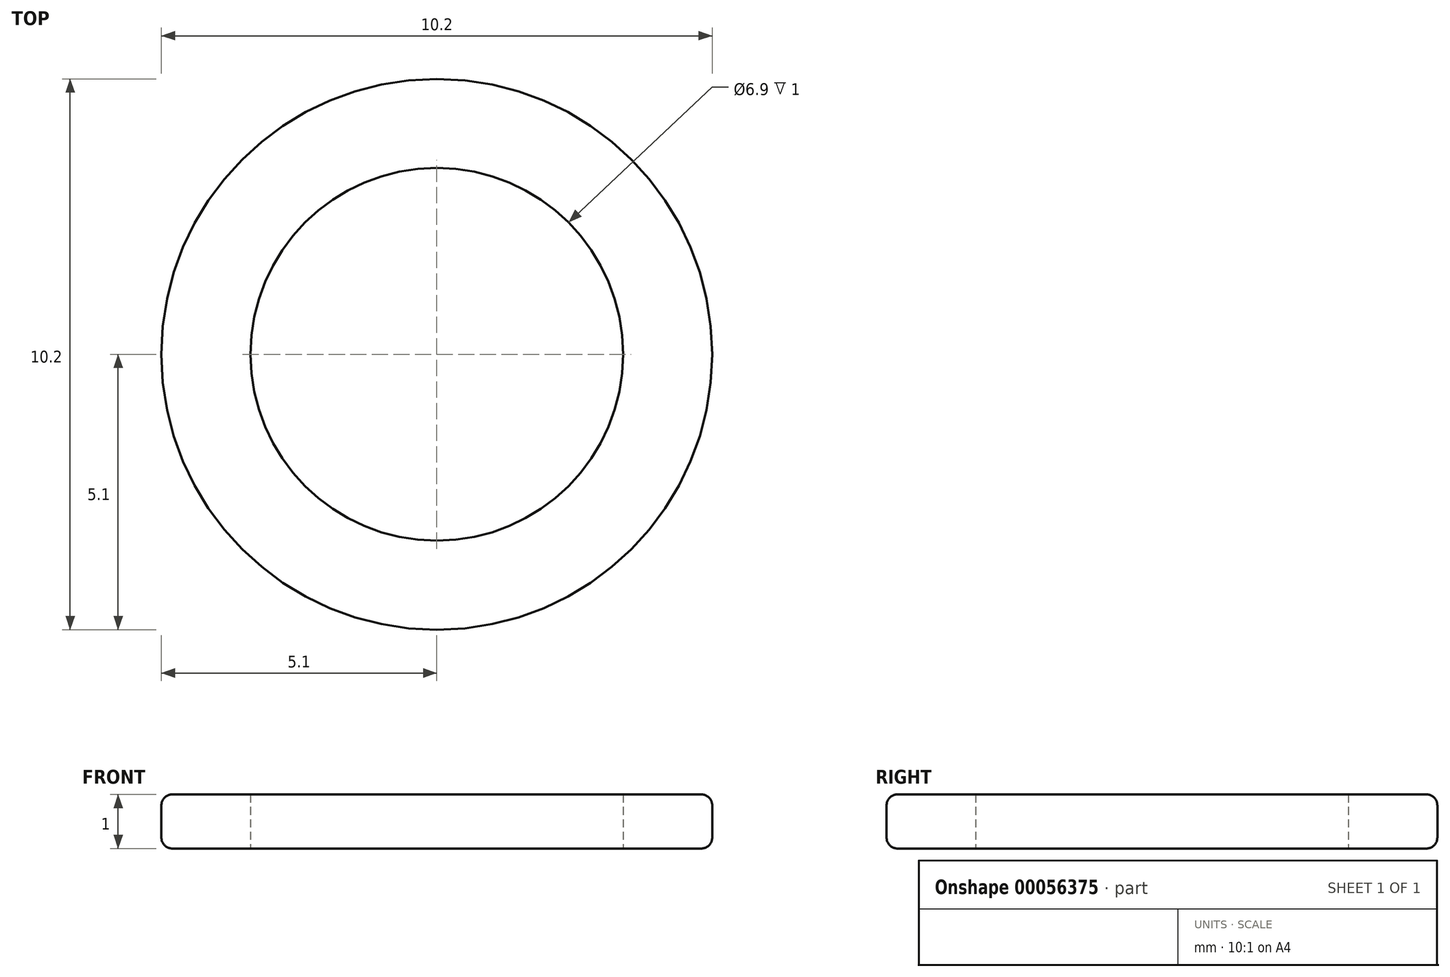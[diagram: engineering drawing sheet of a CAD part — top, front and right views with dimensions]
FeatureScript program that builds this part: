
annotation { "Feature Type Name" : "Feature", "Feature Type Description" : "" }
export const myFeature = defineFeature(function(context is Context, id is Id, definition is map)
    precondition{}
    {
        {
            var Q0;
            Q0=qCreatedBy(makeId("Top.planeOp"),FACE);
            var sketch = newSketch(context, id + "F0", { "sketchPlane" : qUnion([Q0])});
            skCircle(sketch, "E0", {"center": v(0, 0) * mm, "radius": 5.1 * mm});
            skCircle(sketch, "E1", {"center": v(0, 0) * mm, "radius": 3.45 * mm});
            skSolve(sketch);
        }
        {
            var Q0;
            Q0=makeQuery(id+"F0.imprint","IMPRINT",FACE,{"disambiguationData":[TD([[makeQuery(id+"F0.imprint","IMPRINT",EDGE,{"derivedFrom":sQuery(id+"F0.wireOp",EDGE,"E0")}),1.0]])]});
            extrude(context, id + "F1", {"entities" : qUnion([Q0]), "depth" : 1 * mm, "offsetDistance" : 25 * mm});
        }
        {
            var Q0;
            Q0=makeQuery(id+"F1.opExtrude","CAP_EDGE",EDGE,{"disambiguationData":[OSD([sQuery(id+"F0.wireOp",EDGE,"E0")])],"isStart":false});
            var Q1;
            Q1=makeQuery(id+"F1.opExtrude","CAP_EDGE",EDGE,{"disambiguationData":[OSD([sQuery(id+"F0.wireOp",EDGE,"E0")])],"isStart":true});
            fillet(context, id + "F2", {"entities" : qUnion([Q0, Q1]), "radius" : 0.2 * mm, "tangentPropagation" : true, "allowEdgeOverflow" : false});
        }
    });
